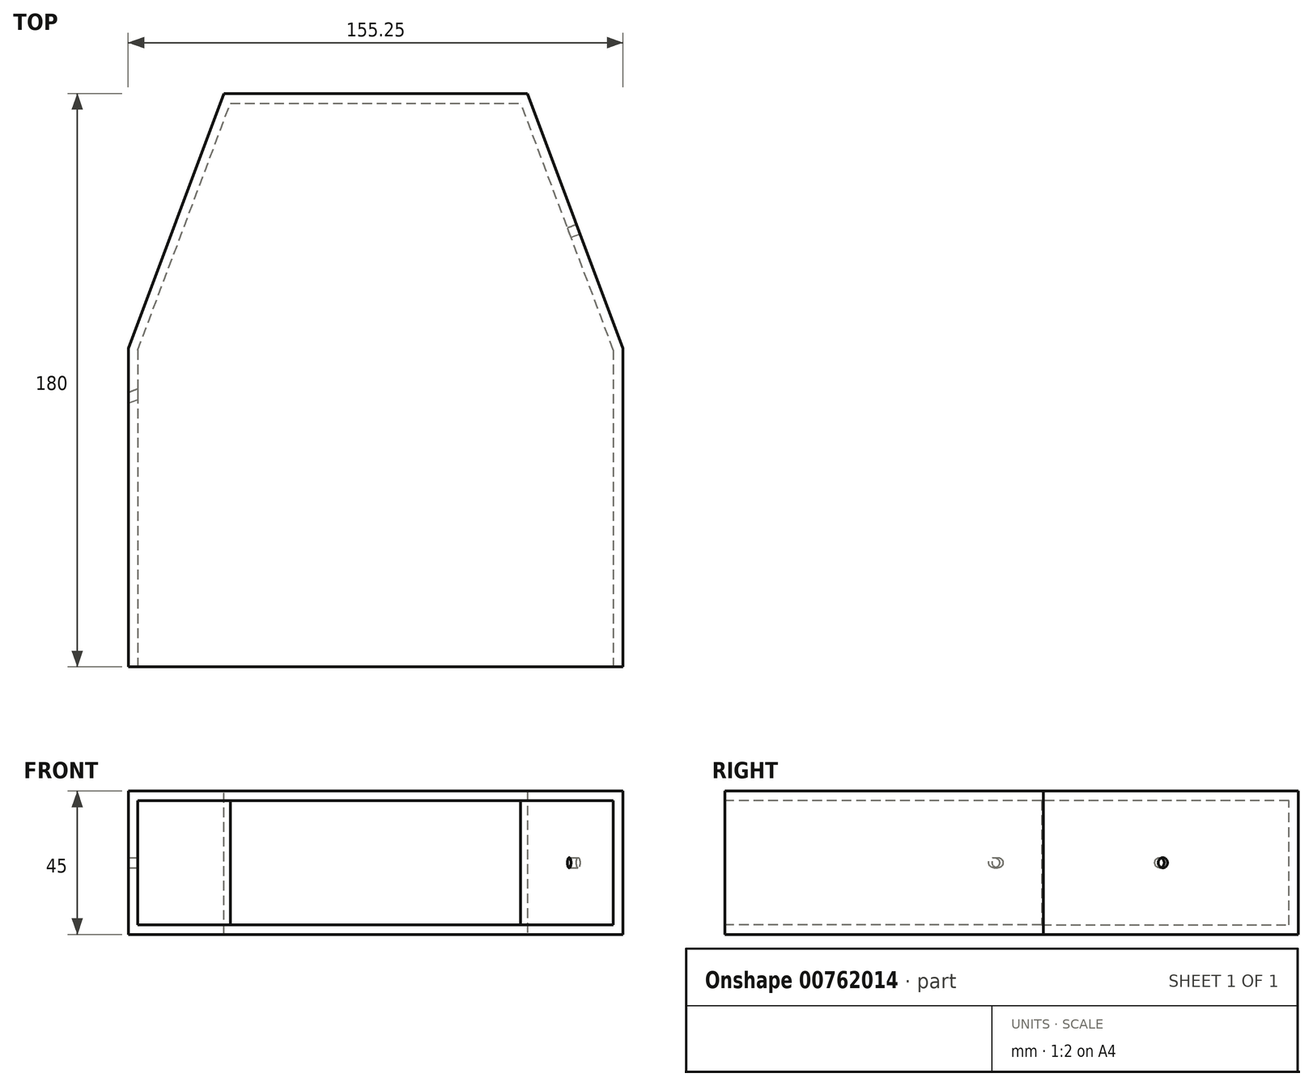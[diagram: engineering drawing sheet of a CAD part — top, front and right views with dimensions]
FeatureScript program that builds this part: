
annotation { "Feature Type Name" : "Feature", "Feature Type Description" : "" }
export const myFeature = defineFeature(function(context is Context, id is Id, definition is map)
    precondition{}
    {
        {
            var Q0;
            Q0=qCreatedBy(makeId("Top.planeOp"),FACE);
            var sketch = newSketch(context, id + "F0", { "sketchPlane" : qUnion([Q0])});
            skLineSegment(sketch, "E0.bottom", {"start": v(-97.62, 74.07) * mm, "end": v(57.63, 74.07) * mm});
            skLineSegment(sketch, "E0.top", {"start": v(-97.62, -105.93) * mm, "end": v(57.63, -105.93) * mm});
            skLineSegment(sketch, "E0.left", {"start": v(-97.62, 74.07) * mm, "end": v(-97.62, -105.93) * mm});
            skLineSegment(sketch, "E0.right", {"start": v(57.63, 74.07) * mm, "end": v(57.63, -105.93) * mm});
            skSolve(sketch);
        }
        {
            var Q0;
            {var subQ0=sQuery(id+"F0.wireOp",EDGE,"E0.top");Q0=makeQuery(id+"F0.imprint","IMPRINT",FACE,{"disambiguationData":[TD([[makeQuery(id+"F0.imprint","IMPRINT",EDGE,{"derivedFrom":subQ0}),1.0]])]});}
            extrude(context, id + "F1", {"entities" : qUnion([Q0]), "oppositeDirection" : true, "depth" : 45 * mm, "offsetDistance" : 25.4 * mm});
        }
        {
            var Q0;
            Q0=makeQuery(id+"F1.opExtrude","SWEPT_EDGE",EDGE,{"disambiguationData":[OSD([sQuery(id+"F0.wireOp",EDGE,"E0.bottom"),sQuery(id+"F0.wireOp",EDGE,"E0.left")])]});
            chamfer(context, id + "F2", {"entities" : qUnion([Q0]), "chamferType" : ChamferType.TWO_OFFSETS, "width1" : 30 * mm, "oppositeDirection" : false, "width2" : 80 * mm, "tangentPropagation" : true});
        }
        {
            var Q0;
            Q0=makeQuery(id+"F1.opExtrude","SWEPT_EDGE",EDGE,{"disambiguationData":[OSD([sQuery(id+"F0.wireOp",EDGE,"E0.bottom"),sQuery(id+"F0.wireOp",EDGE,"E0.right")])]});
            chamfer(context, id + "F3", {"entities" : qUnion([Q0]), "chamferType" : ChamferType.TWO_OFFSETS, "width1" : 80 * mm, "oppositeDirection" : false, "width2" : 30 * mm, "tangentPropagation" : true});
        }
        {
            var Q0;
            Q0=makeQuery(id+"F1.opExtrude","SWEPT_FACE",FACE,{"disambiguationData":[OSD([sQuery(id+"F0.wireOp",EDGE,"E0.top")])]});
            shell(context, id + "F4", {"entities" : qUnion([Q0]), "thickness" : 3 * mm});
        }
        {
            var Q0;
            Q0=makeQuery(id+"F3.opChamfer","BLEND_FACE",FACE,{"disambiguationData":[OSD([sQuery(id+"F0.wireOp",EDGE,"E0.bottom"),sQuery(id+"F0.wireOp",EDGE,"E0.right")])]});
            var sketch = newSketch(context, id + "F5", { "sketchPlane" : qUnion([Q0])});
            skPoint(sketch, "E1.endSnap0", {"position": v(59.65, -22.5) * mm});
            skLineSegment(sketch, "E2", {"start": v(-25.8, -22.5) * mm, "end": v(59.65, -22.5) * mm});
            skLineSegment(sketch, "E3", {"start": v(14.2, 0) * mm, "end": v(14.2, -45) * mm});
            skCircle(sketch, "E4", {"center": v(14.2, -22.5) * mm, "radius": 1.59 * mm});
            skSolve(sketch);
        }
        {
            var Q0;
            Q0=sQuery(id+"F5.wireOp",VERTEX,"E4.center");
            var Q1;
            Q1=makeQuery(id+"F1.opExtrude","SWEPT_BODY",BODY,{"disambiguationData":[OSD([sQuery(id+"F0.wireOp",EDGE,"E0.bottom"),sQuery(id+"F0.wireOp",EDGE,"E0.top"),sQuery(id+"F0.wireOp",EDGE,"E0.left"),sQuery(id+"F0.wireOp",EDGE,"E0.right")])]});
            hole(context, id + "F6", {"style" : HoleStyle.SIMPLE, "endStyle" : HoleEndStyle.THROUGH, "holeDiameter" : 3.17 * mm, "majorDiameter" : 6.35 * mm, "isTappedThrough" : true, "tappedDepth" : 12.7 * mm, "tapClearance" : 3, "locations" : qUnion([Q0]), "scope" : qUnion([Q1])});
        }
    });
